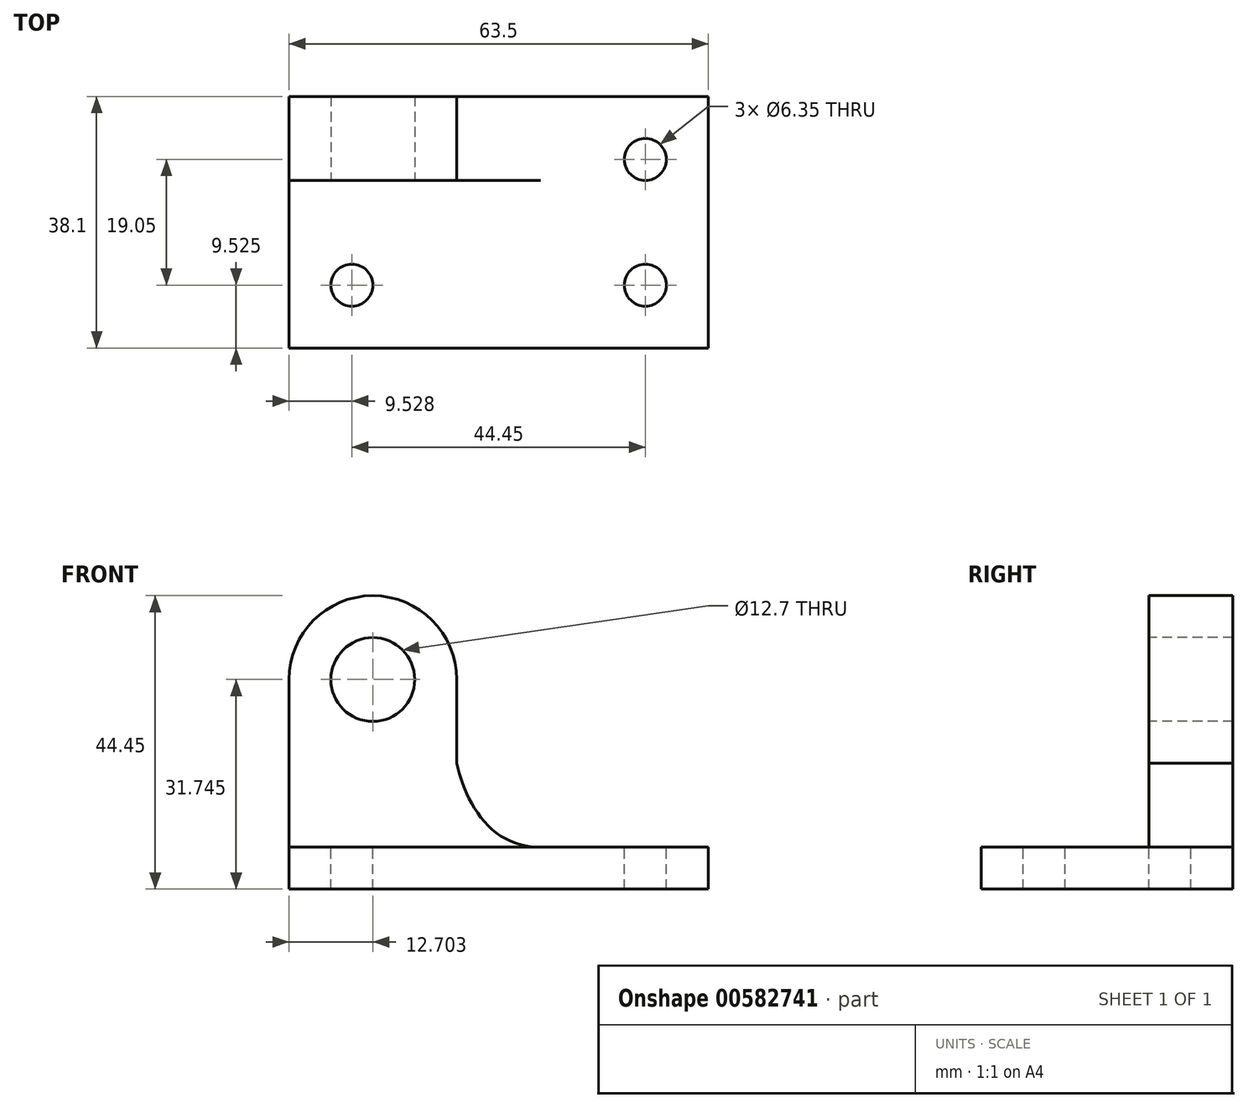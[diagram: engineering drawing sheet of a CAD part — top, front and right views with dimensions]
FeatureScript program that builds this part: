
annotation { "Feature Type Name" : "Feature", "Feature Type Description" : "" }
export const myFeature = defineFeature(function(context is Context, id is Id, definition is map)
    precondition{}
    {
        {
            var Q0;
            Q0=qCreatedBy(makeId("Front.planeOp"),FACE);
            var sketch = newSketch(context, id + "F0", { "sketchPlane" : qUnion([Q0])});
            skLineSegment(sketch, "E0", {"start": v(-59.42, 10.83) * mm, "end": v(4.08, 10.83) * mm});
            skLineSegment(sketch, "E1", {"start": v(4.08, 10.83) * mm, "end": v(4.08, 17.18) * mm});
            skLineSegment(sketch, "E2", {"start": v(4.08, 17.18) * mm, "end": v(-34.02, 17.18) * mm});
            skLineSegment(sketch, "E3", {"start": v(-34.02, 17.18) * mm, "end": v(-34.02, 42.58) * mm});
            skLineSegment(sketch, "E4", {"start": v(-34.02, 42.58) * mm, "end": v(-59.42, 42.58) * mm});
            skLineSegment(sketch, "E5", {"start": v(-59.42, 42.58) * mm, "end": v(-59.42, 10.83) * mm});
            skLineSegment(sketch, "E6", {"start": v(-59.42, 10.83) * mm, "end": v(-59.42, 10.83) * mm});
            skArc(sketch, "E7", {"start": v(-34.02, 42.58) * mm, "mid": v(-46.72, 55.28) * mm, "end": v(-59.42, 42.58) * mm});
            skFitSpline(sketch, "E8", {"points": [v(-34.02, 42.58) * mm, v(-34.02, 29.88) * mm, v(-21.32, 17.18) * mm], "startDerivative": vector(-3.92, -26.47) * mm, "endDerivative": vector(43.22, 0) * mm});
            skSolve(sketch);
        }
        {
            var Q0;
            Q0 = qSketchRegion(id + "F0", true);
            extrude(context, id + "F1", {"entities" : qUnion([Q0]), "depth" : 12.7 * mm, "offsetDistance" : 25.4 * mm});
        }
        {
            var Q0;
            Q0=makeQuery(id+"F1.opExtrude","CAP_FACE",FACE,{"disambiguationData":[OSD([sQuery(id+"F0.wireOp",EDGE,"E0"),sQuery(id+"F0.wireOp",EDGE,"E1"),sQuery(id+"F0.wireOp",EDGE,"E2"),sQuery(id+"F0.wireOp",EDGE,"E3"),sQuery(id+"F0.wireOp",EDGE,"E5"),sQuery(id+"F0.wireOp",EDGE,"E7"),sQuery(id+"F0.wireOp",EDGE,"E8")])],"isStart":false});
            var sketch = newSketch(context, id + "F2", { "sketchPlane" : qUnion([Q0])});
            skLineSegment(sketch, "E9", {"start": v(-21.32, 17.18) * mm, "end": v(-59.42, 17.18) * mm});
            skSolve(sketch);
        }
        {
            var Q0;
            {var subQ1=sQuery(id+"F2.wireOp",EDGE,"E9");Q0=makeQuery(id+"F2.imprint","IMPRINT",FACE,{"disambiguationData":[TD([[makeQuery(id+"F2.imprint","IMPRINT",EDGE,{"derivedFrom":subQ1}),1.0]])]});}
            extrude(context, id + "F3", {"entities" : qUnion([Q0]), "operationType" : NewBodyOperationType.ADD, "depth" : 25.4 * mm, "offsetDistance" : 25.4 * mm});
        }
        {
            var Q0;
            Q0=makeQuery(id+"F1.opExtrude","CAP_FACE",FACE,{"disambiguationData":[OSD([sQuery(id+"F0.wireOp",EDGE,"E0"),sQuery(id+"F0.wireOp",EDGE,"E1"),sQuery(id+"F0.wireOp",EDGE,"E2"),sQuery(id+"F0.wireOp",EDGE,"E3"),sQuery(id+"F0.wireOp",EDGE,"E5"),sQuery(id+"F0.wireOp",EDGE,"E7"),sQuery(id+"F0.wireOp",EDGE,"E8")])],"isStart":false});
            var sketch = newSketch(context, id + "F4", { "sketchPlane" : qUnion([Q0])});
            skCircle(sketch, "E10", {"center": v(-46.72, 42.58) * mm, "radius": 6.35 * mm});
            skSolve(sketch);
        }
        {
            var Q0;
            Q0 = qSketchRegion(id + "F4", true);
            extrude(context, id + "F5", {"entities" : qUnion([Q0]), "operationType" : NewBodyOperationType.REMOVE, "oppositeDirection" : true, "depth" : 25.4 * mm, "offsetDistance" : 25.4 * mm});
        }
        {
            var Q0;
            {var subQ0=sQuery(id+"F0.wireOp",EDGE,"E2");Q0=makeQuery(id+"F3.boolean.opBoolean","MERGE",FACE,{"derivedFrom":[makeQuery(id+"F1.opExtrude","SWEPT_FACE",FACE,{"disambiguationData":[OSD([subQ0])]}),makeQuery(id+"F3.opExtrude","SWEPT_FACE",FACE,{"disambiguationData":[OSD([subQ0,sQuery(id+"F2.wireOp",EDGE,"E9")])]})]});}
            var sketch = newSketch(context, id + "F6", { "sketchPlane" : qUnion([Q0])});
            skCircle(sketch, "E11", {"center": v(-49.9, -28.58) * mm, "radius": 3.18 * mm});
            skCircle(sketch, "E12", {"center": v(-5.44, -28.58) * mm, "radius": 3.18 * mm});
            skCircle(sketch, "E13", {"center": v(-5.44, -9.53) * mm, "radius": 3.18 * mm});
            skSolve(sketch);
        }
        {
            var Q0;
            Q0 = qSketchRegion(id + "F6", true);
            extrude(context, id + "F7", {"entities" : qUnion([Q0]), "operationType" : NewBodyOperationType.REMOVE, "oppositeDirection" : true, "depth" : 25.4 * mm, "offsetDistance" : 25.4 * mm});
        }
    });
